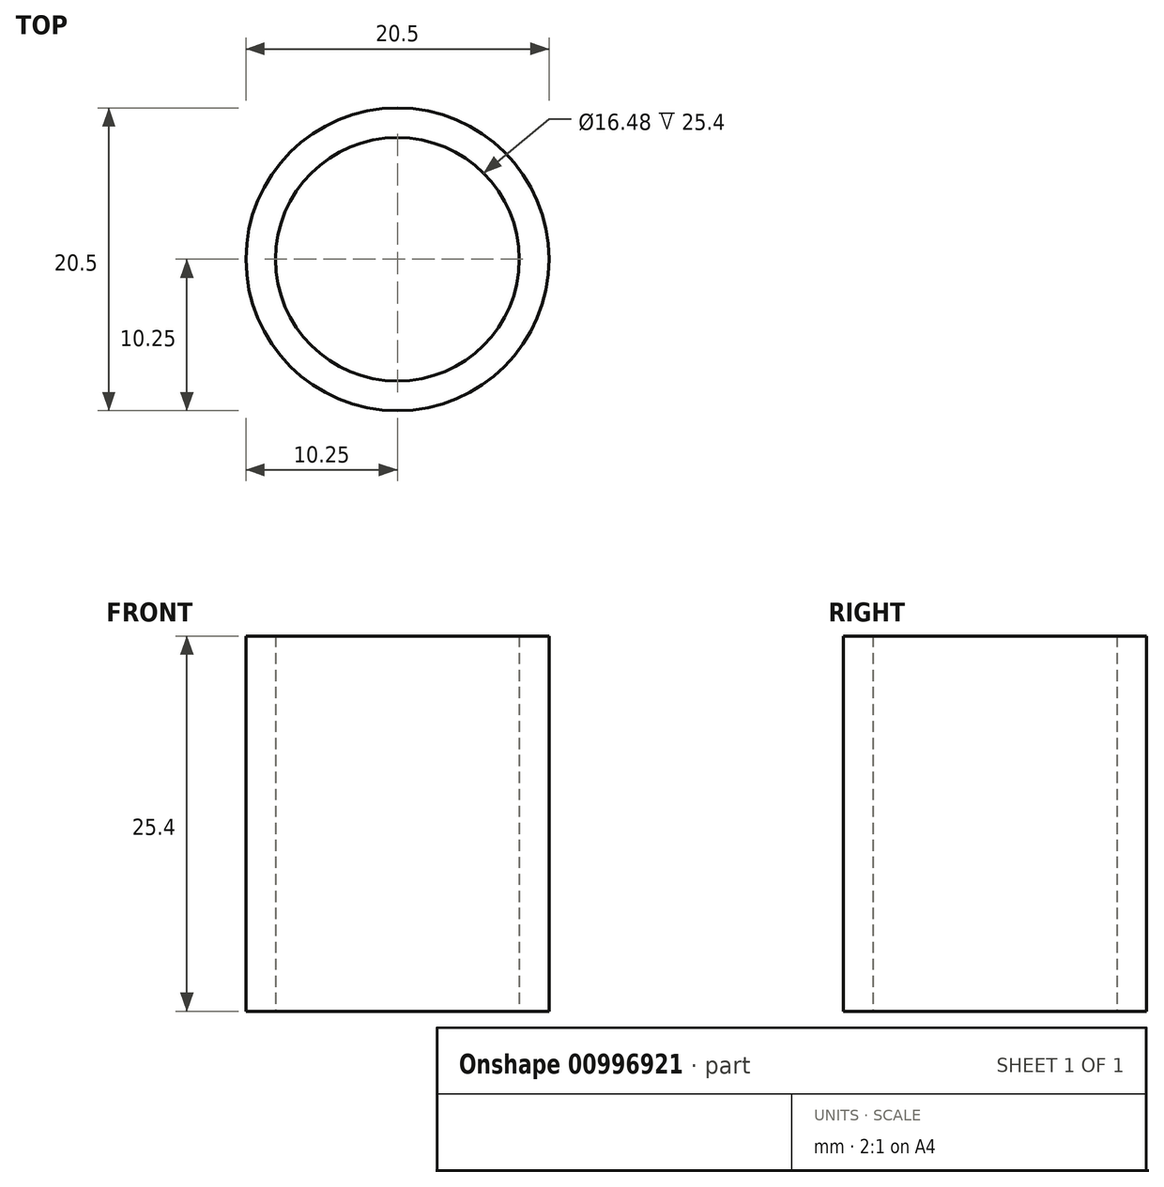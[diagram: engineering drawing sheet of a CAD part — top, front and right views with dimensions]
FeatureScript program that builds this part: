
annotation { "Feature Type Name" : "Feature", "Feature Type Description" : "" }
export const myFeature = defineFeature(function(context is Context, id is Id, definition is map)
    precondition{}
    {
        {
            var Q0;
            Q0=qCreatedBy(makeId("Top.planeOp"),FACE);
            var sketch = newSketch(context, id + "F0", { "sketchPlane" : qUnion([Q0])});
            skCircle(sketch, "E0", {"center": v(0, 0) * mm, "radius": 10.25 * mm});
            skCircle(sketch, "E1", {"center": v(0, 0) * mm, "radius": 8.24 * mm});
            skSolve(sketch);
        }
        {
            var Q0;
            Q0 = qSketchRegion(id + "F0", true);
            extrude(context, id + "F1", {"entities" : qUnion([Q0]), "depth" : 25.4 * mm, "offsetDistance" : 25.4 * mm});
        }
    });
